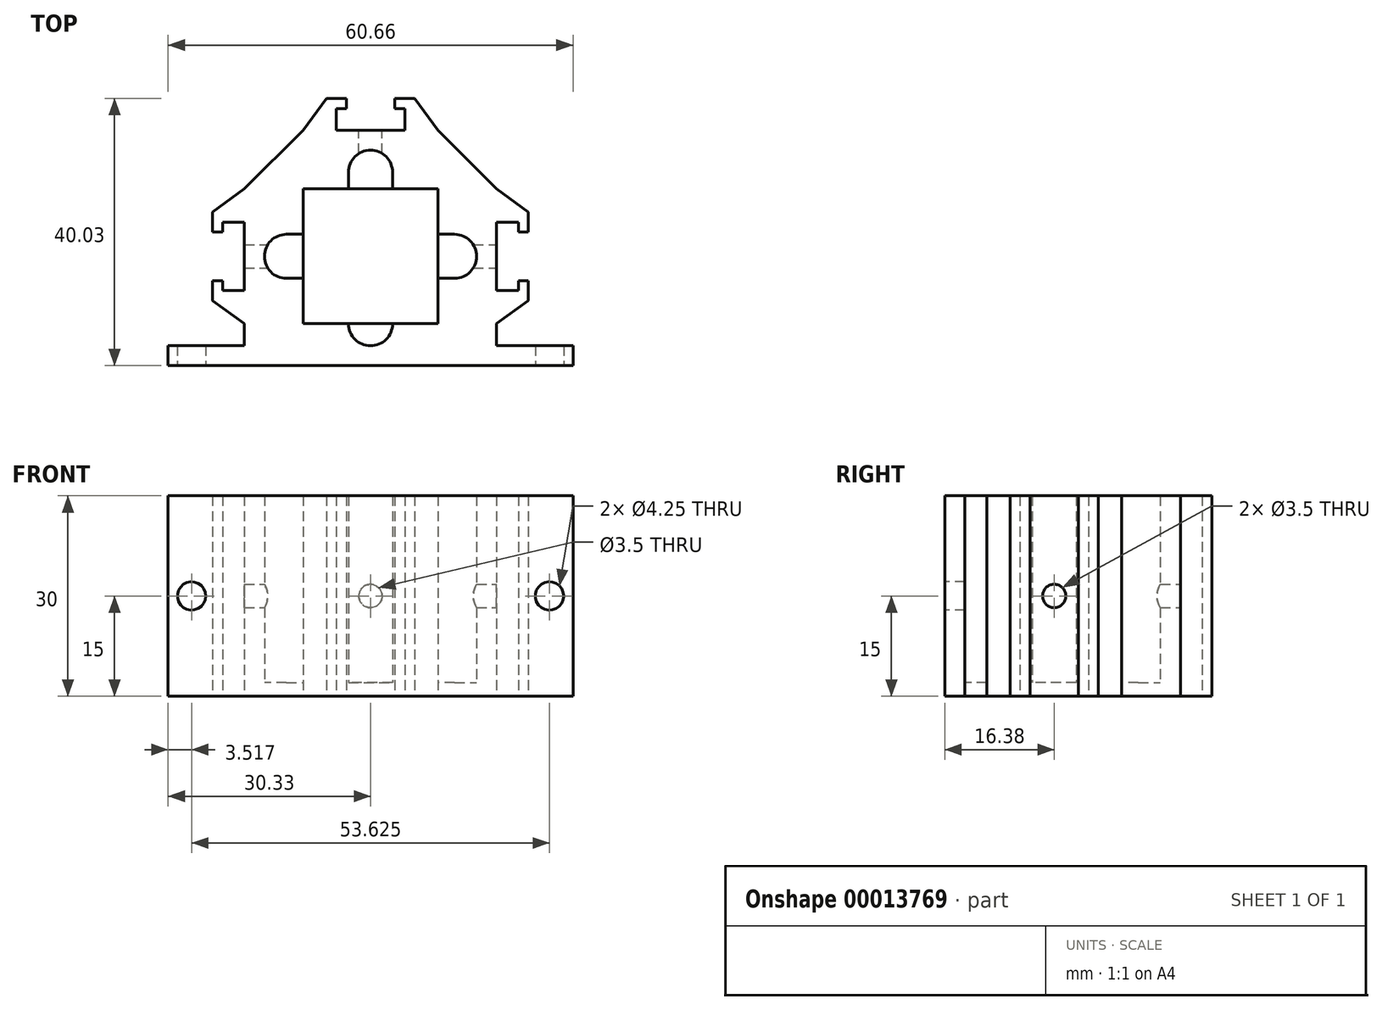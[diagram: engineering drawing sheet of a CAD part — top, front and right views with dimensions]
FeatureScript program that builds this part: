
annotation { "Feature Type Name" : "Feature", "Feature Type Description" : "" }
export const myFeature = defineFeature(function(context is Context, id is Id, definition is map)
    precondition{}
    {
        {
            var Q0;
            Q0=qCreatedBy(makeId("Top.planeOp"),FACE);
            var sketch = newSketch(context, id + "F0", { "sketchPlane" : qUnion([Q0])});
            skLineSegment(sketch, "E0.rect.bottom", {"start": v(10.1, -10.1) * mm, "end": v(-10.1, -10.1) * mm, "construction": true});
            skLineSegment(sketch, "E0.rect.top", {"start": v(10.1, 10.1) * mm, "end": v(-10.1, 10.1) * mm, "construction": true});
            skLineSegment(sketch, "E0.rect.left", {"start": v(10.1, -10.1) * mm, "end": v(10.1, 10.1) * mm, "construction": true});
            skLineSegment(sketch, "E0.rect.right", {"start": v(-10.1, -10.1) * mm, "end": v(-10.1, 10.1) * mm, "construction": true});
            skPoint(sketch, "E0.rect.middle", {"position": v(0, 0) * mm});
            skArc(sketch, "E1", {"start": v(-3.3, -10.1) * mm, "mid": v(0, -13.4) * mm, "end": v(3.3, -10.1) * mm});
            skArc(sketch, "E2", {"start": v(3.3, 12.6) * mm, "mid": v(0, 15.9) * mm, "end": v(-3.3, 12.6) * mm});
            skLineSegment(sketch, "E3", {"start": v(-3.3, 10.1) * mm, "end": v(-3.3, 12.6) * mm});
            skLineSegment(sketch, "E4", {"start": v(3.3, 10.1) * mm, "end": v(3.3, 12.6) * mm});
            skLineSegment(sketch, "E5", {"start": v(-3.3, 10.1) * mm, "end": v(-3.54, 10.1) * mm});
            skLineSegment(sketch, "E6", {"start": v(-10.1, 18.9) * mm, "end": v(-6.62, 18.9) * mm});
            skLineSegment(sketch, "E7.0.MirrorCS", {"start": v(10.1, 18.9) * mm, "end": v(6.62, 18.9) * mm});
            skPoint(sketch, "E8.center.orphan", {"position": v(0, 10.1) * mm});
            skLineSegment(sketch, "E9", {"start": v(-6.62, 18.9) * mm, "end": v(-6.63, 23.65) * mm});
            skLineSegment(sketch, "E10", {"start": v(-6.63, 23.65) * mm, "end": v(-3.62, 23.65) * mm});
            skLineSegment(sketch, "E11", {"start": v(-3.62, 23.65) * mm, "end": v(-3.62, 22.15) * mm});
            skLineSegment(sketch, "E12", {"start": v(-3.62, 22.15) * mm, "end": v(-5.12, 22.15) * mm});
            skLineSegment(sketch, "E13", {"start": v(-5.12, 22.15) * mm, "end": v(-5.12, 18.9) * mm});
            skLineSegment(sketch, "E14.0.MirrorCS", {"start": v(6.63, 23.65) * mm, "end": v(3.62, 23.65) * mm});
            skLineSegment(sketch, "E15.0.MirrorCS", {"start": v(3.62, 23.65) * mm, "end": v(3.62, 22.15) * mm});
            skLineSegment(sketch, "E16.0.MirrorCS", {"start": v(3.62, 22.15) * mm, "end": v(5.12, 22.15) * mm});
            skLineSegment(sketch, "E17.0.MirrorCS", {"start": v(5.12, 22.15) * mm, "end": v(5.12, 18.9) * mm});
            skLineSegment(sketch, "E18.0.MirrorCS", {"start": v(6.63, 18.9) * mm, "end": v(6.63, 23.65) * mm});
            skLineSegment(sketch, "E19.trimOffspring", {"start": v(-5.12, 18.9) * mm, "end": v(0, 18.9) * mm});
            skLineSegment(sketch, "E20.trimOffspring", {"start": v(5.12, 18.9) * mm, "end": v(0, 18.9) * mm});
            skLineSegment(sketch, "E21.1.0", {"start": v(18.9, 6.63) * mm, "end": v(23.65, 6.63) * mm});
            skLineSegment(sketch, "E21.1.3", {"start": v(18.9, 5.12) * mm, "end": v(18.9, 0) * mm});
            skLineSegment(sketch, "E21.1.4", {"start": v(10.1, -3.3) * mm, "end": v(10.1, -10.1) * mm});
            skLineSegment(sketch, "E21.1.5", {"start": v(23.65, -6.63) * mm, "end": v(23.65, -3.63) * mm});
            skArc(sketch, "E21.1.6", {"start": v(12.6, -3.3) * mm, "mid": v(15.9, 0) * mm, "end": v(12.6, 3.3) * mm});
            skLineSegment(sketch, "E21.1.7", {"start": v(10.1, 3.3) * mm, "end": v(10.1, 10.1) * mm});
            skLineSegment(sketch, "E21.1.8", {"start": v(23.65, 6.63) * mm, "end": v(23.65, 3.62) * mm});
            skLineSegment(sketch, "E21.1.9", {"start": v(18.9, 10.1) * mm, "end": v(18.9, 6.63) * mm});
            skLineSegment(sketch, "E21.1.10", {"start": v(18.9, -10.1) * mm, "end": v(18.9, -6.63) * mm});
            skLineSegment(sketch, "E21.1.11", {"start": v(22.15, 5.12) * mm, "end": v(18.9, 5.12) * mm});
            skLineSegment(sketch, "E21.1.12", {"start": v(18.9, -5.13) * mm, "end": v(18.9, 0) * mm});
            skLineSegment(sketch, "E21.1.13", {"start": v(18.9, -6.63) * mm, "end": v(23.65, -6.63) * mm});
            skLineSegment(sketch, "E21.1.14", {"start": v(22.15, -5.13) * mm, "end": v(18.9, -5.13) * mm});
            skLineSegment(sketch, "E21.1.15", {"start": v(22.15, 3.62) * mm, "end": v(22.15, 5.12) * mm});
            skLineSegment(sketch, "E21.1.16", {"start": v(22.15, -3.63) * mm, "end": v(22.15, -5.13) * mm});
            skLineSegment(sketch, "E21.1.17", {"start": v(23.65, -3.63) * mm, "end": v(22.15, -3.63) * mm});
            skLineSegment(sketch, "E21.1.18", {"start": v(10.1, 3.3) * mm, "end": v(12.6, 3.3) * mm});
            skLineSegment(sketch, "E21.1.19", {"start": v(10.1, -3.3) * mm, "end": v(12.6, -3.3) * mm});
            skLineSegment(sketch, "E21.1.20", {"start": v(23.65, 3.62) * mm, "end": v(22.15, 3.62) * mm});
            skLineSegment(sketch, "E21.anchor1", {"start": v(0, 0) * mm, "end": v(-6.63, 18.9) * mm, "construction": true});
            skLineSegment(sketch, "E21.anchor2", {"start": v(0, 0) * mm, "end": v(18.9, 6.63) * mm, "construction": true});
            skLineSegment(sketch, "E22.1.0", {"start": v(-18.9, -10.1) * mm, "end": v(-18.9, -6.63) * mm});
            skLineSegment(sketch, "E22.1.1", {"start": v(-18.9, 10.1) * mm, "end": v(-18.9, 6.62) * mm});
            skArc(sketch, "E22.1.3", {"start": v(-12.6, 3.3) * mm, "mid": v(-15.9, 0) * mm, "end": v(-12.6, -3.3) * mm});
            skLineSegment(sketch, "E22.1.4", {"start": v(-18.9, -6.63) * mm, "end": v(-23.65, -6.63) * mm});
            skLineSegment(sketch, "E22.1.5", {"start": v(-18.9, -5.13) * mm, "end": v(-18.9, 0) * mm});
            skLineSegment(sketch, "E22.1.7", {"start": v(-18.9, 5.12) * mm, "end": v(-18.9, 0) * mm});
            skLineSegment(sketch, "E22.1.8", {"start": v(-18.9, 6.62) * mm, "end": v(-23.65, 6.62) * mm});
            skLineSegment(sketch, "E22.1.9", {"start": v(-10.1, -3.3) * mm, "end": v(-10.1, -10.1) * mm});
            skLineSegment(sketch, "E22.1.10", {"start": v(-22.15, 5.12) * mm, "end": v(-18.9, 5.12) * mm});
            skLineSegment(sketch, "E22.1.11", {"start": v(-22.15, -5.13) * mm, "end": v(-18.9, -5.13) * mm});
            skLineSegment(sketch, "E22.1.12", {"start": v(-23.65, 6.62) * mm, "end": v(-23.65, 3.62) * mm});
            skLineSegment(sketch, "E22.1.13", {"start": v(-23.65, -6.63) * mm, "end": v(-23.65, -3.63) * mm});
            skLineSegment(sketch, "E22.1.15", {"start": v(-23.65, 3.62) * mm, "end": v(-22.15, 3.62) * mm});
            skLineSegment(sketch, "E22.1.16", {"start": v(-10.1, 3.3) * mm, "end": v(-12.6, 3.3) * mm});
            skLineSegment(sketch, "E22.1.17", {"start": v(-22.15, 3.62) * mm, "end": v(-22.15, 5.12) * mm});
            skLineSegment(sketch, "E22.1.18", {"start": v(-23.65, -3.63) * mm, "end": v(-22.15, -3.63) * mm});
            skLineSegment(sketch, "E22.1.19", {"start": v(-22.15, -3.63) * mm, "end": v(-22.15, -5.13) * mm});
            skLineSegment(sketch, "E22.1.20", {"start": v(-10.1, -3.3) * mm, "end": v(-12.6, -3.3) * mm});
            skLineSegment(sketch, "E22.anchor2", {"start": v(0, 0) * mm, "end": v(-18.9, -6.63) * mm, "construction": true});
            skLineSegment(sketch, "E23", {"start": v(-18.9, 10.1) * mm, "end": v(-10.1, 18.9) * mm});
            skLineSegment(sketch, "E24", {"start": v(10.1, 18.9) * mm, "end": v(18.9, 10.1) * mm});
            skLineSegment(sketch, "E25", {"start": v(-18.9, -10.1) * mm, "end": v(-18.9, -16.38) * mm});
            skLineSegment(sketch, "E26", {"start": v(-18.9, -16.38) * mm, "end": v(0, -16.38) * mm});
            skLineSegment(sketch, "E27.0.MirrorCS", {"start": v(18.9, -16.38) * mm, "end": v(0, -16.38) * mm});
            skLineSegment(sketch, "E28.0.MirrorCS", {"start": v(18.9, -10.1) * mm, "end": v(18.9, -16.38) * mm});
            skLineSegment(sketch, "E29", {"start": v(-10.1, -10.1) * mm, "end": v(-3.3, -10.1) * mm});
            skLineSegment(sketch, "E30", {"start": v(10.1, -10.1) * mm, "end": v(3.3, -10.1) * mm});
            skLineSegment(sketch, "E31", {"start": v(-10.1, 3.3) * mm, "end": v(-10.1, 10.1) * mm});
            skLineSegment(sketch, "E32", {"start": v(-3.3, 10.1) * mm, "end": v(-10.1, 10.1) * mm});
            skLineSegment(sketch, "E33", {"start": v(3.3, 10.1) * mm, "end": v(10.1, 10.1) * mm});
            skLineSegment(sketch, "E34", {"start": v(-10.1, 18.9) * mm, "end": v(-6.63, 23.65) * mm});
            skLineSegment(sketch, "E35", {"start": v(10.1, 18.9) * mm, "end": v(6.63, 23.65) * mm});
            skLineSegment(sketch, "E36", {"start": v(18.9, 10.1) * mm, "end": v(23.65, 6.63) * mm});
            skLineSegment(sketch, "E37", {"start": v(23.65, -6.63) * mm, "end": v(18.9, -10.1) * mm});
            skLineSegment(sketch, "E38", {"start": v(-23.65, 6.62) * mm, "end": v(-18.9, 10.1) * mm});
            skLineSegment(sketch, "E39", {"start": v(-23.65, -6.63) * mm, "end": v(-18.9, -10.1) * mm});
            skSolve(sketch);
        }
        {
            var Q0;
            Q0 = qSketchRegion(id + "F0", true);
            var Q1;
            Q1=makeQuery(id+"F0.imprint","IMPRINT",FACE,{"disambiguationData":[TD([[makeQuery(id+"F0.imprint","IMPRINT",EDGE,{"derivedFrom":sQuery(id+"F0.wireOp",EDGE,"E1")}),1.0]])]});
            extrude(context, id + "F1", {"entities" : qUnion([Q0, Q1]), "depth" : 2 * mm});
        }
        {
            var Q0;
            Q0 = qSketchRegion(id + "F0", true);
            extrude(context, id + "F2", {"entities" : qUnion([Q0]), "operationType" : NewBodyOperationType.ADD, "depth" : 30 * mm});
        }
        {
            var Q0;
            Q0=makeQuery(id+"F1.opExtrude","CAP_FACE",FACE,{"disambiguationData":[OSD([sQuery(id+"F0.wireOp",EDGE,"E6"),sQuery(id+"F0.wireOp",EDGE,"E7.0.MirrorCS"),sQuery(id+"F0.wireOp",EDGE,"E9"),sQuery(id+"F0.wireOp",EDGE,"E10"),sQuery(id+"F0.wireOp",EDGE,"E11"),sQuery(id+"F0.wireOp",EDGE,"E12"),sQuery(id+"F0.wireOp",EDGE,"E13"),sQuery(id+"F0.wireOp",EDGE,"E14.0.MirrorCS"),sQuery(id+"F0.wireOp",EDGE,"E15.0.MirrorCS"),sQuery(id+"F0.wireOp",EDGE,"E16.0.MirrorCS"),sQuery(id+"F0.wireOp",EDGE,"E17.0.MirrorCS"),sQuery(id+"F0.wireOp",EDGE,"E18.0.MirrorCS"),sQuery(id+"F0.wireOp",EDGE,"E19.trimOffspring"),sQuery(id+"F0.wireOp",EDGE,"E20.trimOffspring"),sQuery(id+"F0.wireOp",EDGE,"E21.1.0"),sQuery(id+"F0.wireOp",EDGE,"E21.1.3"),sQuery(id+"F0.wireOp",EDGE,"E21.1.5"),sQuery(id+"F0.wireOp",EDGE,"E21.1.8"),sQuery(id+"F0.wireOp",EDGE,"E21.1.9"),sQuery(id+"F0.wireOp",EDGE,"E21.1.10"),sQuery(id+"F0.wireOp",EDGE,"E21.1.11"),sQuery(id+"F0.wireOp",EDGE,"E21.1.12"),sQuery(id+"F0.wireOp",EDGE,"E21.1.13"),sQuery(id+"F0.wireOp",EDGE,"E21.1.14"),sQuery(id+"F0.wireOp",EDGE,"E21.1.15"),sQuery(id+"F0.wireOp",EDGE,"E21.1.16"),sQuery(id+"F0.wireOp",EDGE,"E21.1.17"),sQuery(id+"F0.wireOp",EDGE,"E21.1.20"),sQuery(id+"F0.wireOp",EDGE,"E22.1.0"),sQuery(id+"F0.wireOp",EDGE,"E22.1.1"),sQuery(id+"F0.wireOp",EDGE,"E22.1.4"),sQuery(id+"F0.wireOp",EDGE,"E22.1.5"),sQuery(id+"F0.wireOp",EDGE,"E22.1.7"),sQuery(id+"F0.wireOp",EDGE,"E22.1.8"),sQuery(id+"F0.wireOp",EDGE,"E22.1.10"),sQuery(id+"F0.wireOp",EDGE,"E22.1.11"),sQuery(id+"F0.wireOp",EDGE,"E22.1.12"),sQuery(id+"F0.wireOp",EDGE,"E22.1.13"),sQuery(id+"F0.wireOp",EDGE,"E22.1.15"),sQuery(id+"F0.wireOp",EDGE,"E22.1.17"),sQuery(id+"F0.wireOp",EDGE,"E22.1.18"),sQuery(id+"F0.wireOp",EDGE,"E22.1.19"),sQuery(id+"F0.wireOp",EDGE,"E23"),sQuery(id+"F0.wireOp",EDGE,"E24"),sQuery(id+"F0.wireOp",EDGE,"E25"),sQuery(id+"F0.wireOp",EDGE,"E26"),sQuery(id+"F0.wireOp",EDGE,"E27.0.MirrorCS"),sQuery(id+"F0.wireOp",EDGE,"E28.0.MirrorCS")])],"isStart":false});
            var sketch = newSketch(context, id + "F3", { "sketchPlane" : qUnion([Q0])});
            skLineSegment(sketch, "E40", {"start": v(-10.1, 10.1) * mm, "end": v(10.1, 10.1) * mm});
            skLineSegment(sketch, "E41", {"start": v(10.1, 10.1) * mm, "end": v(10.1, -10.1) * mm});
            skLineSegment(sketch, "E42", {"start": v(10.1, -10.1) * mm, "end": v(-10.1, -10.1) * mm});
            skLineSegment(sketch, "E43", {"start": v(-10.1, -10.1) * mm, "end": v(-10.1, 10.1) * mm});
            skSolve(sketch);
        }
        {
            var Q0;
            Q0 = qSketchRegion(id + "F3", true);
            extrude(context, id + "F4", {"entities" : qUnion([Q0]), "operationType" : NewBodyOperationType.REMOVE, "endBound" : BoundingType.THROUGH_ALL, "oppositeDirection" : true, "depth" : 25 * mm});
        }
        {
            var Q0;
            {var subQ0=sQuery(id+"F0.wireOp",EDGE,"E19.trimOffspring");var subQ1=sQuery(id+"F0.wireOp",EDGE,"E20.trimOffspring");Q0=makeQuery(id+"F2.boolean.opBoolean","MERGE",FACE,{"derivedFrom":[makeQuery(id+"F1.opExtrude","SWEPT_FACE",FACE,{"disambiguationData":[OSD([subQ0,subQ1])]}),makeQuery(id+"F2.opExtrude","SWEPT_FACE",FACE,{"disambiguationData":[OSD([subQ0,subQ1])]})]});}
            var sketch = newSketch(context, id + "F5", { "sketchPlane" : qUnion([Q0])});
            skLineSegment(sketch, "E44", {"start": v(0, 30) * mm, "end": v(0, 0) * mm, "construction": true});
            skCircle(sketch, "E45", {"center": v(0, 15) * mm, "radius": 1.75 * mm});
            skSolve(sketch);
        }
        {
            var Q0;
            Q0 = qSketchRegion(id + "F5", true);
            extrude(context, id + "F6", {"entities" : qUnion([Q0]), "operationType" : NewBodyOperationType.REMOVE, "endBound" : BoundingType.UP_TO_NEXT, "oppositeDirection" : true, "depth" : 25 * mm});
        }
        {
            var Q0;
            {var subQ0=sQuery(id+"F0.wireOp",EDGE,"E21.1.3");var subQ1=sQuery(id+"F0.wireOp",EDGE,"E21.1.12");Q0=makeQuery(id+"F2.boolean.opBoolean","MERGE",FACE,{"derivedFrom":[makeQuery(id+"F1.opExtrude","SWEPT_FACE",FACE,{"disambiguationData":[OSD([subQ0,subQ1])]}),makeQuery(id+"F2.opExtrude","SWEPT_FACE",FACE,{"disambiguationData":[OSD([subQ0,subQ1])]})]});}
            var sketch = newSketch(context, id + "F7", { "sketchPlane" : qUnion([Q0])});
            skLineSegment(sketch, "E46", {"start": v(0, 30) * mm, "end": v(0, 0) * mm, "construction": true});
            skCircle(sketch, "E47", {"center": v(0, 15) * mm, "radius": 1.75 * mm});
            skSolve(sketch);
        }
        {
            var Q0;
            Q0 = qSketchRegion(id + "F7", true);
            extrude(context, id + "F8", {"entities" : qUnion([Q0]), "operationType" : NewBodyOperationType.REMOVE, "endBound" : BoundingType.THROUGH_ALL, "oppositeDirection" : true, "depth" : 25 * mm});
        }
        {
            var Q0;
            {var subQ0=sQuery(id+"F0.wireOp",EDGE,"E26");var subQ1=sQuery(id+"F0.wireOp",EDGE,"E27.0.MirrorCS");Q0=makeQuery(id+"F2.boolean.opBoolean","MERGE",FACE,{"derivedFrom":[makeQuery(id+"F1.opExtrude","SWEPT_FACE",FACE,{"disambiguationData":[OSD([subQ0,subQ1])]}),makeQuery(id+"F2.opExtrude","SWEPT_FACE",FACE,{"disambiguationData":[OSD([subQ0,subQ1])]})]});}
            var sketch = newSketch(context, id + "F9", { "sketchPlane" : qUnion([Q0])});
            skLineSegment(sketch, "E48.bottom", {"start": v(-18.9, 30) * mm, "end": v(-30.33, 30) * mm});
            skLineSegment(sketch, "E48.top", {"start": v(-18.9, 0) * mm, "end": v(-30.33, 0) * mm});
            skLineSegment(sketch, "E48.left", {"start": v(-18.9, 30) * mm, "end": v(-18.9, 0) * mm});
            skLineSegment(sketch, "E48.right", {"start": v(-30.33, 30) * mm, "end": v(-30.33, 0) * mm});
            skLineSegment(sketch, "E49.0.MirrorCS", {"start": v(18.9, 30) * mm, "end": v(30.33, 30) * mm});
            skLineSegment(sketch, "E50.0.MirrorCS", {"start": v(18.9, 30) * mm, "end": v(18.9, 0) * mm});
            skLineSegment(sketch, "E51.0.MirrorCS", {"start": v(18.9, 0) * mm, "end": v(30.33, 0) * mm});
            skLineSegment(sketch, "E52.0.MirrorCS", {"start": v(30.33, 30) * mm, "end": v(30.33, 0) * mm});
            skCircle(sketch, "E53", {"center": v(-26.81, 15) * mm, "radius": 2.12 * mm});
            skCircle(sketch, "E54.0.MirrorC", {"center": v(26.81, 15) * mm, "radius": 2.12 * mm});
            skSolve(sketch);
        }
        {
            var Q0;
            Q0 = qSketchRegion(id + "F9", true);
            extrude(context, id + "F10", {"entities" : qUnion([Q0]), "operationType" : NewBodyOperationType.ADD, "oppositeDirection" : true, "depth" : 3 * mm});
        }
    });
